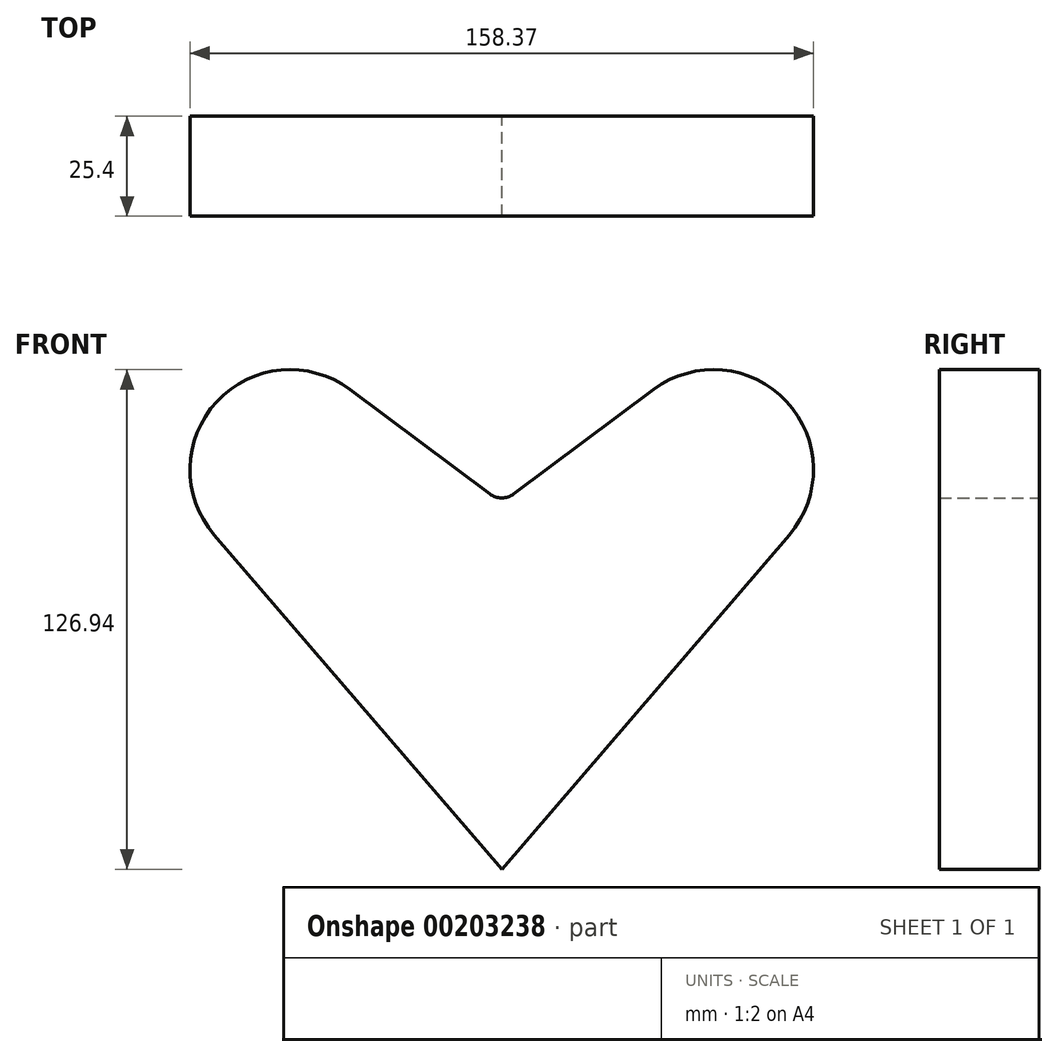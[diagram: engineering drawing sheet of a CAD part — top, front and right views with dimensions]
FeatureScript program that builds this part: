
annotation { "Feature Type Name" : "Feature", "Feature Type Description" : "" }
export const myFeature = defineFeature(function(context is Context, id is Id, definition is map)
    precondition{}
    {
        {
            var Q0;
            Q0=qCreatedBy(makeId("Front.planeOp"),FACE);
            var sketch = newSketch(context, id + "F0", { "sketchPlane" : qUnion([Q0])});
            skArc(sketch, "E0", {"start": v(-43.77, 20.36) * mm, "mid": v(-77.53, 17.33) * mm, "end": v(-78.22, -16.56) * mm});
            skArc(sketch, "E1", {"start": v(67.87, -16.56) * mm, "mid": v(67.18, 17.33) * mm, "end": v(33.43, 20.36) * mm});
            skLineSegment(sketch, "E2", {"start": v(-78.22, -16.56) * mm, "end": v(-5.17, -101.54) * mm});
            skLineSegment(sketch, "E3", {"start": v(67.87, -16.56) * mm, "end": v(-5.17, -101.54) * mm});
            skLineSegment(sketch, "E4", {"start": v(-43.77, 20.36) * mm, "end": v(-5.17, -8.44) * mm});
            skLineSegment(sketch, "E5", {"start": v(33.43, 20.36) * mm, "end": v(-5.17, -8.44) * mm});
            skSolve(sketch);
        }
        {
            var Q0;
            Q0 = qSketchRegion(id + "F0", true);
            extrude(context, id + "F1", {"entities" : qUnion([Q0]), "depth" : 25.4 * mm});
        }
        {
            var Q0;
            Q0 = qSketchRegion(id + "F0", true);
            extrude(context, id + "F2", {"entities" : qUnion([Q0]), "operationType" : NewBodyOperationType.ADD, "depth" : 25.4 * mm});
        }
        {
            var Q0;
            Q0=makeQuery(id+"F1.opExtrude","SWEPT_EDGE",EDGE,{"disambiguationData":[OSD([sQuery(id+"F0.wireOp",EDGE,"E4"),sQuery(id+"F0.wireOp",EDGE,"E5")])]});
            fillet(context, id + "F3", {"entities" : qUnion([Q0]), "radius" : 5.08 * mm, "tangentPropagation" : true, "allowEdgeOverflow" : false});
        }
    });
